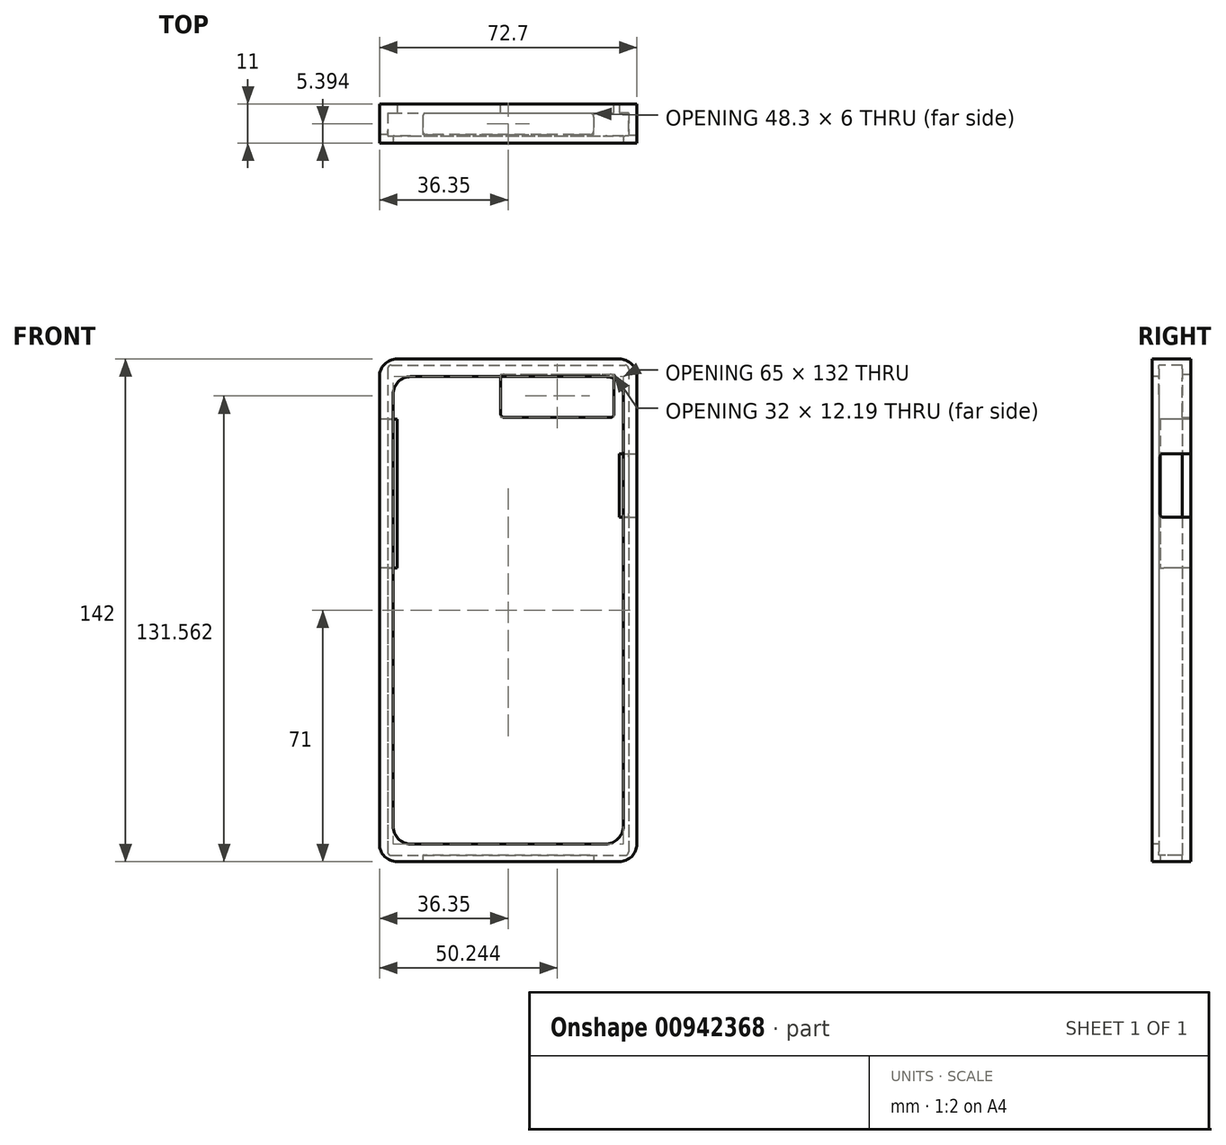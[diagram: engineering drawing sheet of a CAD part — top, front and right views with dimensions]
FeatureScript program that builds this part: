
annotation { "Feature Type Name" : "Feature", "Feature Type Description" : "" }
export const myFeature = defineFeature(function(context is Context, id is Id, definition is map)
    precondition{}
    {
        {
            var Q0;
            Q0=qCreatedBy(makeId("Front.planeOp"),FACE);
            var sketch = newSketch(context, id + "F0", { "sketchPlane" : qUnion([Q0])});
            skLineSegment(sketch, "E0.bottom", {"start": v(-31.35, 71) * mm, "end": v(31.35, 71) * mm});
            skLineSegment(sketch, "E0.top", {"start": v(-31.35, -71) * mm, "end": v(31.35, -71) * mm});
            skLineSegment(sketch, "E0.left", {"start": v(-36.35, 66) * mm, "end": v(-36.35, -66) * mm});
            skLineSegment(sketch, "E0.right", {"start": v(36.35, 66) * mm, "end": v(36.35, -66) * mm});
            skPoint(sketch, "E0.middle", {"position": v(0, 0) * mm});
            skPoint(sketch, "E1.visualSharp", {"position": v(-36.35, 71) * mm});
            skArc(sketch, "E1.filletArc", {"start": v(-31.35, 71) * mm, "mid": v(-34.89, 69.54) * mm, "end": v(-36.35, 66) * mm});
            skPoint(sketch, "E2.visualSharp", {"position": v(36.35, 71) * mm});
            skArc(sketch, "E2.filletArc", {"start": v(36.35, 66) * mm, "mid": v(34.89, 69.54) * mm, "end": v(31.35, 71) * mm});
            skPoint(sketch, "E3.visualSharp", {"position": v(36.35, -71) * mm});
            skArc(sketch, "E3.filletArc", {"start": v(31.35, -71) * mm, "mid": v(34.89, -69.54) * mm, "end": v(36.35, -66) * mm});
            skPoint(sketch, "E4.visualSharp", {"position": v(-36.35, -71) * mm});
            skArc(sketch, "E4.filletArc", {"start": v(-36.35, -66) * mm, "mid": v(-34.89, -69.54) * mm, "end": v(-31.35, -71) * mm});
            skSolve(sketch);
        }
        {
            var Q0;
            Q0 = qSketchRegion(id + "F0", true);
            var Q1;
            Q1=makeQuery(id+"F0.imprint","IMPRINT",FACE,{"disambiguationData":[TD([[makeQuery(id+"F0.imprint","IMPRINT",EDGE,{"derivedFrom":sQuery(id+"F0.wireOp",EDGE,"E0.bottom")}),-1.0]])]});
            extrude(context, id + "F1", {"entities" : qUnion([Q0, Q1]), "depth" : 9 * mm, "offsetDistance" : 25.4 * mm});
        }
        {
            var Q0;
            Q0=makeQuery(id+"F1.opExtrude","CAP_FACE",FACE,{"disambiguationData":[OSD([sQuery(id+"F0.wireOp",EDGE,"E0.bottom"),sQuery(id+"F0.wireOp",EDGE,"E0.top"),sQuery(id+"F0.wireOp",EDGE,"E0.left"),sQuery(id+"F0.wireOp",EDGE,"E0.right")])],"isStart":false});
            var sketch = newSketch(context, id + "F2", { "sketchPlane" : qUnion([Q0])});
            skLineSegment(sketch, "E5.bottom", {"start": v(-33, 69.25) * mm, "end": v(33, 69.25) * mm});
            skLineSegment(sketch, "E5.top", {"start": v(-33, -69.25) * mm, "end": v(33, -69.25) * mm});
            skLineSegment(sketch, "E5.left", {"start": v(-34, 68.25) * mm, "end": v(-34, -68.25) * mm});
            skLineSegment(sketch, "E5.right", {"start": v(34, 68.25) * mm, "end": v(34, -68.25) * mm});
            skPoint(sketch, "E5.middle", {"position": v(0, 0) * mm});
            skPoint(sketch, "E6.visualSharp", {"position": v(-34, 69.25) * mm});
            skArc(sketch, "E6.filletArc", {"start": v(-33, 69.25) * mm, "mid": v(-33.7, 68.96) * mm, "end": v(-34, 68.25) * mm});
            skPoint(sketch, "E7.visualSharp", {"position": v(34, 69.25) * mm});
            skArc(sketch, "E7.filletArc", {"start": v(34, 68.25) * mm, "mid": v(33.7, 68.96) * mm, "end": v(33, 69.25) * mm});
            skPoint(sketch, "E8.visualSharp", {"position": v(34, -69.25) * mm});
            skArc(sketch, "E8.filletArc", {"start": v(33, -69.25) * mm, "mid": v(33.7, -68.96) * mm, "end": v(34, -68.25) * mm});
            skPoint(sketch, "E9.visualSharp", {"position": v(-34, -69.25) * mm});
            skArc(sketch, "E9.filletArc", {"start": v(-34, -68.25) * mm, "mid": v(-33.7, -68.96) * mm, "end": v(-33, -69.25) * mm});
            skSolve(sketch);
        }
        {
            var Q0;
            Q0 = qSketchRegion(id + "F2", true);
            extrude(context, id + "F3", {"entities" : qUnion([Q0]), "operationType" : NewBodyOperationType.REMOVE, "oppositeDirection" : true, "depth" : 6.5 * mm, "offsetDistance" : 25.4 * mm});
        }
        {
            var Q0;
            Q0=makeQuery(id+"F1.opExtrude","SWEPT_FACE",FACE,{"disambiguationData":[OSD([sQuery(id+"F0.wireOp",EDGE,"E0.right")])]});
            var sketch = newSketch(context, id + "F4", { "sketchPlane" : qUnion([Q0])});
            skLineSegment(sketch, "E10.bottom", {"start": v(-2.83, 26.26) * mm, "end": v(-7.74, 26.26) * mm});
            skLineSegment(sketch, "E10.top", {"start": v(-6.33, 44.26) * mm, "end": v(-7.74, 44.26) * mm});
            skLineSegment(sketch, "E10.left", {"start": v(-3.74, 27.26) * mm, "end": v(-3.74, 43.26) * mm});
            skLineSegment(sketch, "E10.right", {"start": v(-8.74, 27.26) * mm, "end": v(-8.74, 43.26) * mm});
            skPoint(sketch, "E10.middle", {"position": v(-6.24, 35.26) * mm});
            skLineSegment(sketch, "E11", {"start": v(-6.24, 70.2) * mm, "end": v(-6.24, 35.26) * mm});
            skPoint(sketch, "E12.visualSharp", {"position": v(-3.74, 44.26) * mm});
            skPoint(sketch, "E13.visualSharp", {"position": v(-8.74, 44.26) * mm});
            skArc(sketch, "E13.filletArc", {"start": v(-7.74, 44.26) * mm, "mid": v(-8.45, 43.97) * mm, "end": v(-8.74, 43.26) * mm});
            skPoint(sketch, "E14.visualSharp", {"position": v(-8.74, 26.26) * mm});
            skArc(sketch, "E14.filletArc", {"start": v(-8.74, 27.26) * mm, "mid": v(-8.45, 26.56) * mm, "end": v(-7.74, 26.26) * mm});
            skPoint(sketch, "E15.visualSharp", {"position": v(-3.74, 26.26) * mm});
            skArc(sketch, "E16.MirrorCS", {"start": v(1.26, 27.26) * mm, "mid": v(0.97, 26.56) * mm, "end": v(0.26, 26.26) * mm});
            skPoint(sketch, "E17.MirrorP", {"position": v(1.26, 26.26) * mm});
            skLineSegment(sketch, "E18.MirrorCS", {"start": v(-4.65, 26.26) * mm, "end": v(0.26, 26.26) * mm});
            skArc(sketch, "E19.MirrorCS", {"start": v(0.26, 44.26) * mm, "mid": v(0.97, 43.97) * mm, "end": v(1.26, 43.26) * mm});
            skLineSegment(sketch, "E20.MirrorCS", {"start": v(-1.15, 44.26) * mm, "end": v(0.26, 44.26) * mm});
            skLineSegment(sketch, "E21.MirrorCS", {"start": v(1.26, 27.26) * mm, "end": v(1.26, 43.26) * mm});
            skPoint(sketch, "E22.MirrorP", {"position": v(-1.24, 35.26) * mm});
            skPoint(sketch, "E23.MirrorP", {"position": v(1.26, 44.26) * mm});
            skLineSegment(sketch, "E24", {"start": v(-1.15, 44.26) * mm, "end": v(-6.33, 44.26) * mm});
            skLineSegment(sketch, "E25", {"start": v(-2.83, 26.26) * mm, "end": v(-4.65, 26.26) * mm});
            skSolve(sketch);
        }
        {
            var Q0;
            Q0=makeQuery(id+"F4.imprint","IMPRINT",FACE,{"disambiguationData":[TD([[makeQuery(id+"F4.imprint","IMPRINT",EDGE,{"derivedFrom":sQuery(id+"F4.wireOp",EDGE,"E10.bottom")}),-1.0]])]});
            var Q1;
            {var subQ2=sQuery(id+"F4.wireOp",EDGE,"E16.MirrorCS");Q1=makeQuery(id+"F4.imprint","IMPRINT",FACE,{"disambiguationData":[TD([[makeQuery(id+"F4.imprint","IMPRINT",EDGE,{"derivedFrom":subQ2}),-1.0]])]});}
            extrude(context, id + "F5", {"entities" : qUnion([Q0, Q1]), "operationType" : NewBodyOperationType.REMOVE, "oppositeDirection" : true, "depth" : 5 * mm, "offsetDistance" : 25 * mm});
        }
        {
            var Q0;
            Q0=makeQuery(id+"F1.opExtrude","SWEPT_FACE",FACE,{"disambiguationData":[OSD([sQuery(id+"F0.wireOp",EDGE,"E0.left")])]});
            var sketch = newSketch(context, id + "F6", { "sketchPlane" : qUnion([Q0])});
            skLineSegment(sketch, "E26.right", {"start": v(3.34, 12.93) * mm, "end": v(3.34, 52.93) * mm});
            skPoint(sketch, "E26.middle", {"position": v(7.6, 32.93) * mm});
            skPoint(sketch, "E27.visualSharp", {"position": v(3.34, 53.93) * mm});
            skPoint(sketch, "E28.visualSharp", {"position": v(3.34, 11.93) * mm});
            skPoint(sketch, "E29.visualSharp", {"position": v(11.84, 11.93) * mm});
            skArc(sketch, "E29.filletArc", {"start": v(10.84, 11.93) * mm, "mid": v(11.55, 12.22) * mm, "end": v(11.84, 12.93) * mm});
            skArc(sketch, "E30.MirrorCS", {"start": v(-4.16, 11.93) * mm, "mid": v(-4.86, 12.22) * mm, "end": v(-5.16, 12.93) * mm});
            skArc(sketch, "E31.MirrorCS", {"start": v(-5.16, 52.86) * mm, "mid": v(-4.91, 53.58) * mm, "end": v(-4.22, 53.93) * mm});
            skLineSegment(sketch, "E32.MirrorCS", {"start": v(-4.22, 53.93) * mm, "end": v(1.36, 53.93) * mm});
            skLineSegment(sketch, "E33.MirrorCS", {"start": v(-5.16, 12.93) * mm, "end": v(-5.16, 52.86) * mm});
            skLineSegment(sketch, "E34.MirrorCS", {"start": v(-4.16, 11.93) * mm, "end": v(1.36, 11.93) * mm});
            skPoint(sketch, "E35.MirrorP", {"position": v(-0.9, 32.93) * mm});
            skLineSegment(sketch, "E36", {"start": v(5.33, 53.93) * mm, "end": v(1.36, 53.93) * mm});
            skLineSegment(sketch, "E37", {"start": v(5.33, 11.93) * mm, "end": v(1.36, 11.93) * mm});
            skLineSegment(sketch, "E38", {"start": v(5.33, 11.93) * mm, "end": v(7.6, 11.93) * mm});
            skLineSegment(sketch, "E39", {"start": v(5.33, 53.93) * mm, "end": v(6.61, 53.93) * mm});
            skLineSegment(sketch, "E40", {"start": v(6.61, 53.93) * mm, "end": v(8.65, 53.93) * mm});
            skLineSegment(sketch, "E41", {"start": v(8.65, 53.93) * mm, "end": v(8.65, 11.93) * mm});
            skLineSegment(sketch, "E42", {"start": v(8.65, 11.93) * mm, "end": v(7.6, 11.93) * mm});
            skSolve(sketch);
        }
        {
            var Q0;
            {var subQ0=sQuery(id+"F6.wireOp",EDGE,"E36");Q0=makeQuery(id+"F6.imprint","IMPRINT",FACE,{"disambiguationData":[TD([[makeQuery(id+"F6.imprint","IMPRINT",EDGE,{"derivedFrom":subQ0}),1.0]])]});}
            var Q1;
            {var subQ4=sQuery(id+"F6.wireOp",EDGE,"E30.MirrorCS");Q1=makeQuery(id+"F6.imprint","IMPRINT",FACE,{"disambiguationData":[TD([[makeQuery(id+"F6.imprint","IMPRINT",EDGE,{"derivedFrom":subQ4}),-1.0]])]});}
            extrude(context, id + "F7", {"entities" : qUnion([Q0, Q1]), "operationType" : NewBodyOperationType.REMOVE, "oppositeDirection" : true, "depth" : 5 * mm, "offsetDistance" : 25 * mm});
        }
        {
            var Q0;
            Q0=makeQuery(id+"F1.opExtrude","SWEPT_FACE",FACE,{"disambiguationData":[OSD([sQuery(id+"F0.wireOp",EDGE,"E0.top")])]});
            var sketch = newSketch(context, id + "F8", { "sketchPlane" : qUnion([Q0])});
            skLineSegment(sketch, "E43.bottom", {"start": v(23.15, 2.6) * mm, "end": v(-23.15, 2.6) * mm});
            skLineSegment(sketch, "E43.top", {"start": v(23.15, 8.6) * mm, "end": v(-23.15, 8.6) * mm});
            skLineSegment(sketch, "E43.left", {"start": v(24.15, 3.6) * mm, "end": v(24.15, 7.6) * mm});
            skLineSegment(sketch, "E43.right", {"start": v(-24.15, 3.6) * mm, "end": v(-24.15, 7.6) * mm});
            skPoint(sketch, "E43.middle", {"position": v(0, 5.6) * mm});
            skLineSegment(sketch, "E44", {"start": v(-36.35, 5.65) * mm, "end": v(36.23, 5.56) * mm});
            skPoint(sketch, "E45.visualSharp", {"position": v(-24.15, 8.6) * mm});
            skArc(sketch, "E45.filletArc", {"start": v(-23.15, 8.6) * mm, "mid": v(-23.86, 8.31) * mm, "end": v(-24.15, 7.6) * mm});
            skPoint(sketch, "E46.visualSharp", {"position": v(-24.15, 2.6) * mm});
            skArc(sketch, "E46.filletArc", {"start": v(-24.15, 3.6) * mm, "mid": v(-23.86, 2.9) * mm, "end": v(-23.15, 2.6) * mm});
            skPoint(sketch, "E47.visualSharp", {"position": v(24.15, 2.6) * mm});
            skArc(sketch, "E47.filletArc", {"start": v(23.15, 2.6) * mm, "mid": v(23.86, 2.9) * mm, "end": v(24.15, 3.6) * mm});
            skPoint(sketch, "E48.visualSharp", {"position": v(24.15, 8.6) * mm});
            skArc(sketch, "E48.filletArc", {"start": v(24.15, 7.6) * mm, "mid": v(23.86, 8.31) * mm, "end": v(23.15, 8.6) * mm});
            skLineSegment(sketch, "E49", {"start": v(-24.15, 2.6) * mm, "end": v(-31.35, 2.6) * mm});
            skLineSegment(sketch, "E50", {"start": v(24.15, 2.6) * mm, "end": v(31.35, 2.6) * mm});
            skSolve(sketch);
        }
        {
            var Q0;
            Q0=makeQuery(id+"F8.imprint","IMPRINT",FACE,{"disambiguationData":[TD([[makeQuery(id+"F8.imprint","IMPRINT",EDGE,{"derivedFrom":sQuery(id+"F8.wireOp",EDGE,"E43.bottom")}),-1.0]])]});
            var Q1;
            Q1=makeQuery(id+"F8.imprint","IMPRINT",FACE,{"disambiguationData":[TD([[makeQuery(id+"F8.imprint","IMPRINT",EDGE,{"derivedFrom":sQuery(id+"F8.wireOp",EDGE,"E43.top")}),1.0]])]});
            extrude(context, id + "F9", {"entities" : qUnion([Q0, Q1]), "operationType" : NewBodyOperationType.REMOVE, "surfaceOperationType" : NewSurfaceOperationType.ADD, "oppositeDirection" : true, "depth" : 11.3 * mm, "offsetDistance" : 25 * mm});
        }
        {
            var Q0;
            Q0=makeQuery(id+"F1.opExtrude","CAP_FACE",FACE,{"disambiguationData":[OSD([sQuery(id+"F0.wireOp",EDGE,"E0.bottom"),sQuery(id+"F0.wireOp",EDGE,"E0.top"),sQuery(id+"F0.wireOp",EDGE,"E0.left"),sQuery(id+"F0.wireOp",EDGE,"E0.right")])],"isStart":true});
            var sketch = newSketch(context, id + "F10", { "sketchPlane" : qUnion([Q0])});
            skLineSegment(sketch, "E51", {"start": v(-36.35, 54.47) * mm, "end": v(36.35, 54.47) * mm});
            skLineSegment(sketch, "E52", {"start": v(-29.9, 71) * mm, "end": v(-29.9, -71) * mm});
            skLineSegment(sketch, "E53", {"start": v(2.1, 71) * mm, "end": v(2.1, -71) * mm});
            skLineSegment(sketch, "E54.bottom", {"start": v(-28.9, 66.66) * mm, "end": v(1.1, 66.66) * mm});
            skLineSegment(sketch, "E54.top", {"start": v(-28.9, 54.47) * mm, "end": v(1.1, 54.47) * mm});
            skLineSegment(sketch, "E54.left", {"start": v(-29.9, 65.66) * mm, "end": v(-29.9, 55.47) * mm});
            skLineSegment(sketch, "E54.right", {"start": v(2.1, 65.66) * mm, "end": v(2.1, 55.47) * mm});
            skPoint(sketch, "E55.visualSharp", {"position": v(-29.9, 66.66) * mm});
            skArc(sketch, "E55.filletArc", {"start": v(-28.9, 66.66) * mm, "mid": v(-29.6, 66.36) * mm, "end": v(-29.9, 65.66) * mm});
            skPoint(sketch, "E56.visualSharp", {"position": v(2.1, 66.66) * mm});
            skArc(sketch, "E56.filletArc", {"start": v(2.1, 65.66) * mm, "mid": v(1.81, 66.36) * mm, "end": v(1.1, 66.66) * mm});
            skPoint(sketch, "E57.visualSharp", {"position": v(2.1, 54.47) * mm});
            skArc(sketch, "E57.filletArc", {"start": v(1.1, 54.47) * mm, "mid": v(1.81, 54.76) * mm, "end": v(2.1, 55.47) * mm});
            skPoint(sketch, "E58.visualSharp", {"position": v(-29.9, 54.47) * mm});
            skArc(sketch, "E58.filletArc", {"start": v(-29.9, 55.47) * mm, "mid": v(-29.6, 54.76) * mm, "end": v(-28.9, 54.47) * mm});
            skLineSegment(sketch, "E59", {"start": v(2.1, -29.03) * mm, "end": v(2.1, -32.74) * mm});
            skSolve(sketch);
        }
        {
            var Q0;
            Q0=makeQuery(id+"F10.imprint","IMPRINT",FACE,{"disambiguationData":[TD([[makeQuery(id+"F10.imprint","IMPRINT",EDGE,{"derivedFrom":sQuery(id+"F10.wireOp",EDGE,"E54.bottom")}),-1.0]])]});
            extrude(context, id + "F11", {"entities" : qUnion([Q0]), "operationType" : NewBodyOperationType.REMOVE, "oppositeDirection" : true, "depth" : 3 * mm, "offsetDistance" : 25 * mm});
        }
        {
            var Q0;
            Q0=makeQuery(id+"F1.opExtrude","CAP_FACE",FACE,{"disambiguationData":[OSD([sQuery(id+"F0.wireOp",EDGE,"E0.bottom"),sQuery(id+"F0.wireOp",EDGE,"E0.top"),sQuery(id+"F0.wireOp",EDGE,"E0.left"),sQuery(id+"F0.wireOp",EDGE,"E0.right"),sQuery(id+"F0.wireOp",EDGE,"E1.filletArc"),sQuery(id+"F0.wireOp",EDGE,"E2.filletArc"),sQuery(id+"F0.wireOp",EDGE,"E3.filletArc"),sQuery(id+"F0.wireOp",EDGE,"E4.filletArc")])],"isStart":false});
            var sketch = newSketch(context, id + "F12", { "sketchPlane" : qUnion([Q0])});
            skLineSegment(sketch, "E60.bottom", {"start": v(-31.35, 71) * mm, "end": v(31.35, 71) * mm});
            skLineSegment(sketch, "E60.top", {"start": v(-31.35, -71) * mm, "end": v(31.35, -71) * mm});
            skLineSegment(sketch, "E60.left", {"start": v(-36.35, 66) * mm, "end": v(-36.35, -66) * mm});
            skLineSegment(sketch, "E60.right", {"start": v(36.35, 66) * mm, "end": v(36.35, -66) * mm});
            skPoint(sketch, "E60.middle", {"position": v(0, 0) * mm});
            skPoint(sketch, "E61.visualSharp", {"position": v(-36.35, 71) * mm});
            skArc(sketch, "E61.filletArc", {"start": v(-31.35, 71) * mm, "mid": v(-34.89, 69.54) * mm, "end": v(-36.35, 66) * mm});
            skPoint(sketch, "E62.visualSharp", {"position": v(36.35, 71) * mm});
            skArc(sketch, "E62.filletArc", {"start": v(36.35, 66) * mm, "mid": v(34.89, 69.54) * mm, "end": v(31.35, 71) * mm});
            skPoint(sketch, "E63.visualSharp", {"position": v(-36.35, -71) * mm});
            skArc(sketch, "E63.filletArc", {"start": v(-36.35, -66) * mm, "mid": v(-34.89, -69.54) * mm, "end": v(-31.35, -71) * mm});
            skPoint(sketch, "E64.visualSharp", {"position": v(36.35, -71) * mm});
            skArc(sketch, "E64.filletArc", {"start": v(31.35, -71) * mm, "mid": v(34.89, -69.54) * mm, "end": v(36.35, -66) * mm});
            skSolve(sketch);
        }
        {
            var Q0;
            Q0 = qSketchRegion(id + "F12", true);
            extrude(context, id + "F13", {"entities" : qUnion([Q0]), "operationType" : NewBodyOperationType.ADD, "depth" : 2 * mm, "offsetDistance" : 25 * mm});
        }
        {
            var Q0;
            Q0=makeQuery(id+"F13.opExtrude","CAP_FACE",FACE,{"disambiguationData":[OSD([sQuery(id+"F12.wireOp",EDGE,"E60.bottom"),sQuery(id+"F12.wireOp",EDGE,"E60.top"),sQuery(id+"F12.wireOp",EDGE,"E60.left"),sQuery(id+"F12.wireOp",EDGE,"E60.right"),sQuery(id+"F12.wireOp",EDGE,"E61.filletArc"),sQuery(id+"F12.wireOp",EDGE,"E62.filletArc"),sQuery(id+"F12.wireOp",EDGE,"E63.filletArc"),sQuery(id+"F12.wireOp",EDGE,"E64.filletArc")])],"isStart":false});
            var sketch = newSketch(context, id + "F14", { "sketchPlane" : qUnion([Q0])});
            skLineSegment(sketch, "E65.bottom", {"start": v(-23.93, 66) * mm, "end": v(27.5, 66) * mm});
            skLineSegment(sketch, "E65.top", {"start": v(-27.5, -66) * mm, "end": v(27.5, -66) * mm});
            skLineSegment(sketch, "E65.right", {"start": v(32.5, 61) * mm, "end": v(32.5, -61) * mm});
            skPoint(sketch, "E65.middle", {"position": v(0, 0) * mm});
            skPoint(sketch, "E66.visualSharp", {"position": v(-32.5, 66) * mm});
            skPoint(sketch, "E67.visualSharp", {"position": v(32.5, 66) * mm});
            skArc(sketch, "E67.filletArc", {"start": v(32.5, 61) * mm, "mid": v(31.04, 64.54) * mm, "end": v(27.5, 66) * mm});
            skPoint(sketch, "E68.visualSharp", {"position": v(32.5, -66) * mm});
            skArc(sketch, "E68.filletArc", {"start": v(27.5, -66) * mm, "mid": v(31.04, -64.54) * mm, "end": v(32.5, -61) * mm});
            skPoint(sketch, "E69.visualSharp", {"position": v(-32.5, -66) * mm});
            skArc(sketch, "E69.filletArc", {"start": v(-32.5, -61) * mm, "mid": v(-31.04, -64.54) * mm, "end": v(-27.5, -66) * mm});
            skLineSegment(sketch, "E70.bottom", {"start": v(-27.5, 66) * mm, "end": v(27.5, 66) * mm});
            skArc(sketch, "E71.filletArc", {"start": v(-27.5, 66) * mm, "mid": v(-31.04, 64.54) * mm, "end": v(-32.5, 61) * mm});
            skLineSegment(sketch, "E72", {"start": v(-32.5, -61) * mm, "end": v(-32.5, 61) * mm});
            skSolve(sketch);
        }
        {
            var Q0;
            Q0 = qSketchRegion(id + "F14", true);
            extrude(context, id + "F15", {"entities" : qUnion([Q0]), "operationType" : NewBodyOperationType.REMOVE, "oppositeDirection" : true, "depth" : 2 * mm, "offsetDistance" : 25 * mm});
        }
    });
